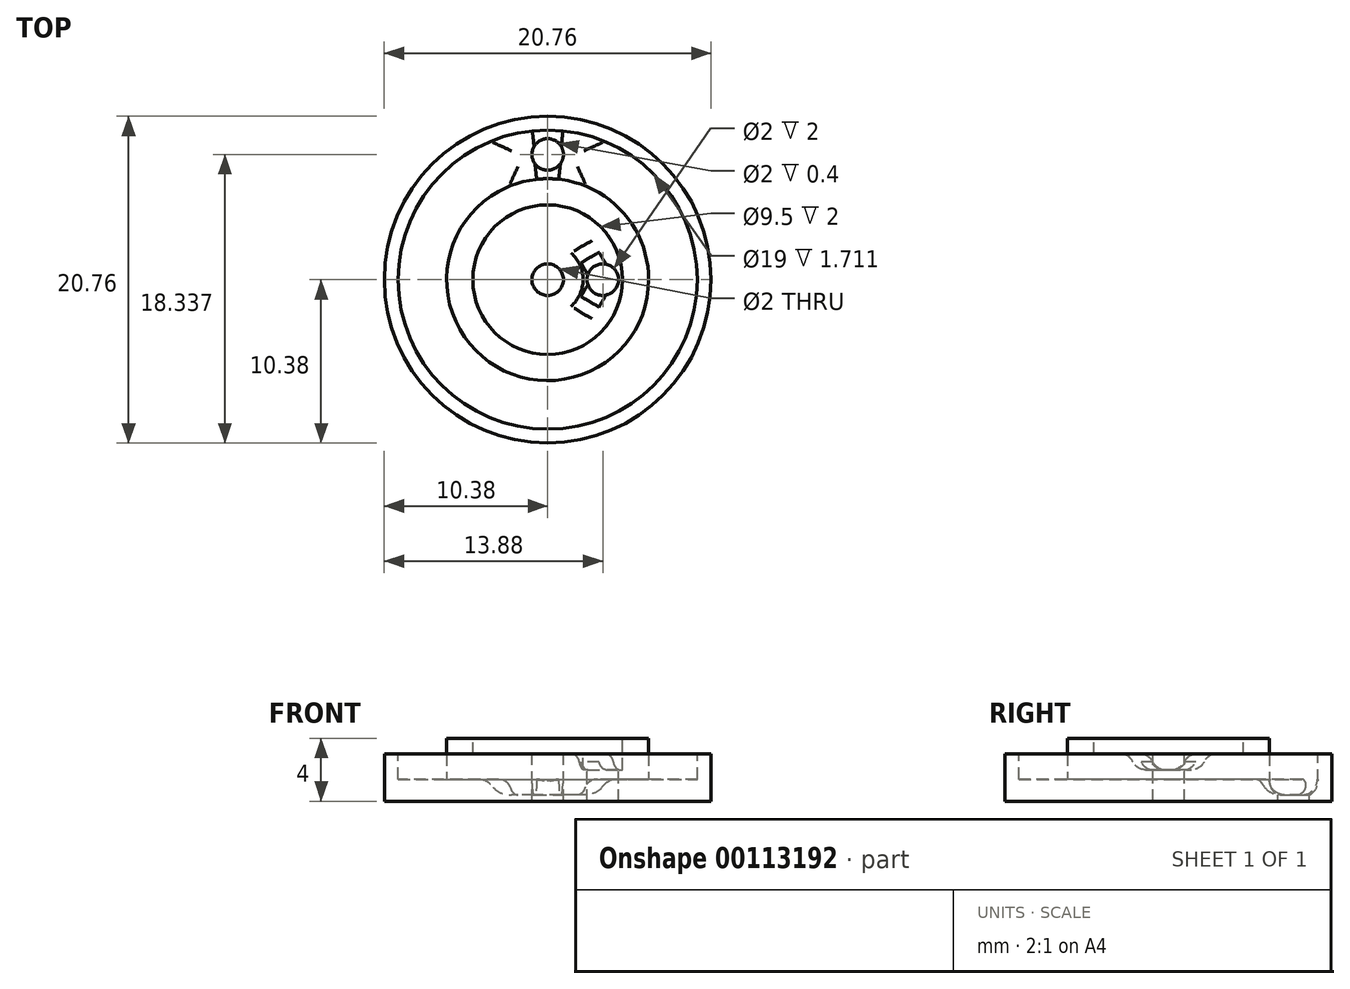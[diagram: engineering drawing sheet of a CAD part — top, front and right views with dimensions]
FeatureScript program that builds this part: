
annotation { "Feature Type Name" : "Feature", "Feature Type Description" : "" }
export const myFeature = defineFeature(function(context is Context, id is Id, definition is map)
    precondition{}
    {
        {
            var Q0;
            Q0=qCreatedBy(makeId("Top.planeOp"),FACE);
            var sketch = newSketch(context, id + "F0", { "sketchPlane" : qUnion([Q0])});
            skCircle(sketch, "E0", {"center": v(0, 0) * mm, "radius": 10.38 * mm});
            skSolve(sketch);
        }
        {
            var Q0;
            Q0=makeQuery(id+"F0.imprint","IMPRINT",FACE,{"disambiguationData":[TD([[makeQuery(id+"F0.imprint","IMPRINT",EDGE,{"derivedFrom":sQuery(id+"F0.wireOp",EDGE,"E0")}),1.0]])]});
            extrude(context, id + "F1", {"entities" : qUnion([Q0]), "depth" : 3 * mm});
        }
        {
            var Q0;
            Q0=makeQuery(id+"F1.opExtrude","CAP_FACE",FACE,{"disambiguationData":[OSD([sQuery(id+"F0.wireOp",EDGE,"E0")])],"isStart":false});
            var sketch = newSketch(context, id + "F2", { "sketchPlane" : qUnion([Q0])});
            skCircle(sketch, "E1", {"center": v(0, 0) * mm, "radius": 9.5 * mm});
            skCircle(sketch, "E2", {"center": v(0, 0) * mm, "radius": 6.41 * mm});
            skCircle(sketch, "E3", {"center": v(0, 0) * mm, "radius": 4.75 * mm});
            skSolve(sketch);
        }
        {
            var Q0;
            Q0=makeQuery(id+"F2.imprint","IMPRINT",FACE,{"disambiguationData":[TD([[makeQuery(id+"F2.imprint","IMPRINT",EDGE,{"derivedFrom":sQuery(id+"F2.wireOp",EDGE,"E2")}),1.0]])]});
            var Q1;
            Q1=makeQuery(id+"F2.imprint","IMPRINT",FACE,{"disambiguationData":[TD([[makeQuery(id+"F2.imprint","IMPRINT",EDGE,{"derivedFrom":sQuery(id+"F2.wireOp",EDGE,"E3")}),1.0]])]});
            extrude(context, id + "F3", {"entities" : qUnion([Q0, Q1]), "operationType" : NewBodyOperationType.ADD, "depth" : 1 * mm});
        }
        {
            var Q0;
            Q0=makeQuery(id+"F3.opExtrude","CAP_FACE",FACE,{"disambiguationData":[OSD([sQuery(id+"F2.wireOp",EDGE,"E2")])],"isStart":false});
            var sketch = newSketch(context, id + "F4", { "sketchPlane" : qUnion([Q0])});
            skCircle(sketch, "E4.0", {"center": v(0, 0) * mm, "radius": 4.75 * mm});
            skSolve(sketch);
        }
        {
            var Q0;
            Q0=makeQuery(id+"F4.imprint","IMPRINT",FACE,{"disambiguationData":[TD([[makeQuery(id+"F4.imprint","IMPRINT",EDGE,{"derivedFrom":sQuery(id+"F4.wireOp",EDGE,"E4.0")}),1.0]])]});
            extrude(context, id + "F5", {"entities" : qUnion([Q0]), "operationType" : NewBodyOperationType.REMOVE, "oppositeDirection" : true, "depth" : 1 * mm});
        }
        {
            var Q0;
            Q0 = qSketchRegion(id + "F2", true);
            extrude(context, id + "F6", {"entities" : qUnion([Q0]), "operationType" : NewBodyOperationType.REMOVE, "oppositeDirection" : true, "depth" : 1.6 * mm});
        }
        {
            var Q0;
            Q0=makeQuery(id+"F5.boolean.opBoolean","COPY",FACE,{"derivedFrom":makeQuery(id+"F5.opExtrude","CAP_FACE",FACE,{"disambiguationData":[OSD([sQuery(id+"F4.wireOp",EDGE,"E4.0")])],"isStart":false})});
            var sketch = newSketch(context, id + "F7", { "sketchPlane" : qUnion([Q0])});
            skCircle(sketch, "E5", {"center": v(0, 0) * mm, "radius": 1 * mm});
            skSolve(sketch);
        }
        {
            var Q0;
            Q0 = qSketchRegion(id + "F7", true);
            extrude(context, id + "F8", {"entities" : qUnion([Q0]), "operationType" : NewBodyOperationType.REMOVE, "endBound" : BoundingType.THROUGH_ALL, "oppositeDirection" : true, "depth" : 25 * mm});
        }
        {
            var Q0;
            Q0=makeQuery(id+"F6.boolean.opBoolean","COPY",FACE,{"derivedFrom":makeQuery(id+"F6.opExtrude","CAP_FACE",FACE,{"disambiguationData":[OSD([sQuery(id+"F2.wireOp",EDGE,"E1"),sQuery(id+"F2.wireOp",EDGE,"E2")])],"isStart":false})});
            var sketch = newSketch(context, id + "F9", { "sketchPlane" : qUnion([Q0])});
            skLineSegment(sketch, "E6", {"start": v(0, 9.5) * mm, "end": v(0, 6.41) * mm, "construction": true});
            skCircle(sketch, "E7", {"center": v(0, 7.96) * mm, "radius": 1 * mm});
            skSolve(sketch);
        }
        {
            var Q0;
            Q0 = qSketchRegion(id + "F9", true);
            extrude(context, id + "F10", {"entities" : qUnion([Q0]), "operationType" : NewBodyOperationType.REMOVE, "endBound" : BoundingType.THROUGH_ALL, "oppositeDirection" : true, "depth" : 25 * mm});
        }
        {
            var Q0;
            Q0=makeQuery(id+"F5.boolean.opBoolean","COPY",FACE,{"derivedFrom":makeQuery(id+"F5.opExtrude","CAP_FACE",FACE,{"disambiguationData":[OSD([sQuery(id+"F4.wireOp",EDGE,"E4.0")])],"isStart":false})});
            var sketch = newSketch(context, id + "F11", { "sketchPlane" : qUnion([Q0])});
            skLineSegment(sketch, "E8", {"start": v(2.25, 0) * mm, "end": v(4.75, 0) * mm, "construction": true});
            skCircle(sketch, "E9", {"center": v(3.5, 0) * mm, "radius": 1 * mm});
            skSolve(sketch);
        }
        {
            var Q0;
            Q0 = qSketchRegion(id + "F11", true);
            extrude(context, id + "F12", {"entities" : qUnion([Q0]), "operationType" : NewBodyOperationType.REMOVE, "endBound" : BoundingType.THROUGH_ALL, "oppositeDirection" : true, "depth" : 25 * mm});
        }
        {
            var Q0;
            Q0=makeQuery(id+"F6.boolean.opBoolean","COPY",FACE,{"derivedFrom":makeQuery(id+"F6.opExtrude","CAP_FACE",FACE,{"disambiguationData":[OSD([sQuery(id+"F2.wireOp",EDGE,"E1"),sQuery(id+"F2.wireOp",EDGE,"E2")])],"isStart":false})});
            var sketch = newSketch(context, id + "F13", { "sketchPlane" : qUnion([Q0])});
            skLineSegment(sketch, "E10", {"start": v(3.64, 8.78) * mm, "end": v(2.45, 5.93) * mm});
            skLineSegment(sketch, "E11", {"start": v(0, 0) * mm, "end": v(-2.45, 5.93) * mm, "construction": true});
            skLineSegment(sketch, "E12", {"start": v(0, 0) * mm, "end": v(0, 8.78) * mm, "construction": true});
            skLineSegment(sketch, "E13", {"start": v(3.64, 8.78) * mm, "end": v(-3.64, 8.78) * mm, "construction": true});
            skLineSegment(sketch, "E14", {"start": v(2.45, 5.93) * mm, "end": v(0, 0) * mm, "construction": true});
            skLineSegment(sketch, "E15", {"start": v(-2.45, 5.93) * mm, "end": v(-3.64, 8.78) * mm});
            skArc(sketch, "E16", {"start": v(3.64, 8.78) * mm, "mid": v(0, 9.5) * mm, "end": v(-3.64, 8.78) * mm});
            skArc(sketch, "E17", {"start": v(-3.64, 8.78) * mm, "mid": v(0, -9.5) * mm, "end": v(3.64, 8.78) * mm, "construction": true});
            skArc(sketch, "E18", {"start": v(-2.45, 5.93) * mm, "mid": v(0, -6.41) * mm, "end": v(2.45, 5.93) * mm, "construction": true});
            skArc(sketch, "E19", {"start": v(2.45, 5.93) * mm, "mid": v(0, 6.41) * mm, "end": v(-2.45, 5.93) * mm});
            skSolve(sketch);
        }
        {
            var Q0;
            Q0=makeQuery(id+"F13.imprint","IMPRINT",FACE,{"disambiguationData":[TD([[makeQuery(id+"F13.imprint","IMPRINT",EDGE,{"derivedFrom":sQuery(id+"F13.wireOp",EDGE,"E10")}),-1.0]])]});
            extrude(context, id + "F14", {"entities" : qUnion([Q0]), "operationType" : NewBodyOperationType.REMOVE, "oppositeDirection" : true, "depth" : 1 * mm});
        }
        {
            var Q0;
            Q0=makeQuery(id+"F5.boolean.opBoolean","COPY",FACE,{"derivedFrom":makeQuery(id+"F5.opExtrude","CAP_FACE",FACE,{"disambiguationData":[OSD([sQuery(id+"F4.wireOp",EDGE,"E4.0")])],"isStart":false})});
            var sketch = newSketch(context, id + "F15", { "sketchPlane" : qUnion([Q0])});
            skCircle(sketch, "E20.0", {"center": v(0, 0) * mm, "radius": 9.5 * mm});
            skCircle(sketch, "E20.1", {"center": v(0, 0) * mm, "radius": 6.41 * mm});
            skLineSegment(sketch, "E21", {"start": v(4.75, 0) * mm, "end": v(2.25, 0) * mm, "construction": true});
            skPoint(sketch, "E22", {"position": v(3.5, 0) * mm});
            skLineSegment(sketch, "E23", {"start": v(4.11, 2.38) * mm, "end": v(1.95, 1.12) * mm});
            skLineSegment(sketch, "E24", {"start": v(0, 0) * mm, "end": v(1.95, -1.12) * mm, "construction": true});
            skLineSegment(sketch, "E25", {"start": v(4.11, -2.37) * mm, "end": v(4.11, 2.37) * mm, "construction": true});
            skLineSegment(sketch, "E26", {"start": v(4.11, 0) * mm, "end": v(0, 0) * mm, "construction": true});
            skArc(sketch, "E27", {"start": v(4.11, 2.37) * mm, "mid": v(-4.75, 0) * mm, "end": v(4.11, -2.38) * mm, "construction": true});
            skArc(sketch, "E28", {"start": v(4.11, -2.37) * mm, "mid": v(4.75, 0) * mm, "end": v(4.11, 2.37) * mm});
            skArc(sketch, "E29", {"start": v(1.95, -1.12) * mm, "mid": v(2.25, 0) * mm, "end": v(1.95, 1.12) * mm});
            skArc(sketch, "E30", {"start": v(1.95, 1.12) * mm, "mid": v(-2.25, 0) * mm, "end": v(1.95, -1.12) * mm, "construction": true});
            skLineSegment(sketch, "E31", {"start": v(1.95, 1.12) * mm, "end": v(0, 0) * mm, "construction": true});
            skLineSegment(sketch, "E32", {"start": v(1.95, -1.12) * mm, "end": v(4.11, -2.37) * mm});
            skSolve(sketch);
        }
        {
            var Q0;
            Q0=makeQuery(id+"F15.imprint","IMPRINT",FACE,{"disambiguationData":[TD([[makeQuery(id+"F15.imprint","IMPRINT",EDGE,{"derivedFrom":sQuery(id+"F15.wireOp",EDGE,"E23")}),1.0]])]});
            extrude(context, id + "F16", {"entities" : qUnion([Q0]), "operationType" : NewBodyOperationType.REMOVE, "oppositeDirection" : true, "depth" : 1 * mm});
        }
        {
            var Q0;
            Q0=makeQuery(id+"F14.boolean.opBoolean","COPY",EDGE,{"derivedFrom":makeQuery(id+"F14.opExtrude","CAP_EDGE",EDGE,{"disambiguationData":[OSD([sQuery(id+"F13.wireOp",EDGE,"E10")])],"isStart":false})});
            var Q1;
            Q1=makeQuery(id+"F14.boolean.opBoolean","COPY",EDGE,{"derivedFrom":makeQuery(id+"F14.opExtrude","CAP_EDGE",EDGE,{"disambiguationData":[OSD([sQuery(id+"F13.wireOp",EDGE,"E16")])],"isStart":false})});
            var Q2;
            Q2=makeQuery(id+"F14.boolean.opBoolean","COPY",EDGE,{"derivedFrom":makeQuery(id+"F14.opExtrude","CAP_EDGE",EDGE,{"disambiguationData":[OSD([sQuery(id+"F13.wireOp",EDGE,"E19")])],"isStart":false})});
            var Q3;
            Q3=makeQuery(id+"F14.boolean.opBoolean","COPY",EDGE,{"derivedFrom":makeQuery(id+"F14.opExtrude","CAP_EDGE",EDGE,{"disambiguationData":[OSD([sQuery(id+"F13.wireOp",EDGE,"E15")])],"isStart":false})});
            var Q4;
            Q4=makeQuery(id+"F16.boolean.opBoolean","COPY",EDGE,{"derivedFrom":makeQuery(id+"F16.opExtrude","CAP_EDGE",EDGE,{"disambiguationData":[OSD([sQuery(id+"F15.wireOp",EDGE,"E32")])],"isStart":false})});
            var Q5;
            Q5=makeQuery(id+"F16.boolean.opBoolean","COPY",EDGE,{"derivedFrom":makeQuery(id+"F16.opExtrude","CAP_EDGE",EDGE,{"disambiguationData":[OSD([sQuery(id+"F15.wireOp",EDGE,"E23")])],"isStart":false})});
            fillet(context, id + "F17", {"entities" : qUnion([Q0, Q1, Q2, Q3, Q4, Q5]), "radius" : 1 * mm, "tangentPropagation" : true, "allowEdgeOverflow" : false});
        }
        {
            var Q0;
            Q0=makeQuery(id+"F17.opFillet","BLEND_EDGE",EDGE,{"blendedFrom":[makeQuery(id+"F14.boolean.opBoolean","COPY",EDGE,{"derivedFrom":makeQuery(id+"F14.opExtrude","CAP_EDGE",EDGE,{"disambiguationData":[OSD([sQuery(id+"F13.wireOp",EDGE,"E10")])],"isStart":false})}),makeQuery(id+"F6.boolean.opBoolean","COPY",FACE,{"derivedFrom":makeQuery(id+"F6.opExtrude","CAP_FACE",FACE,{"disambiguationData":[OSD([sQuery(id+"F2.wireOp",EDGE,"E1"),sQuery(id+"F2.wireOp",EDGE,"E2")])],"isStart":false})})],"blendedInto":[makeQuery(id+"F6.boolean.opBoolean","COPY",FACE,{"derivedFrom":makeQuery(id+"F6.opExtrude","CAP_FACE",FACE,{"disambiguationData":[OSD([sQuery(id+"F2.wireOp",EDGE,"E1"),sQuery(id+"F2.wireOp",EDGE,"E2")])],"isStart":false})})]});
            var Q1;
            Q1=makeQuery(id+"F17.opFillet","BLEND_EDGE",EDGE,{"blendedFrom":[makeQuery(id+"F14.boolean.opBoolean","COPY",EDGE,{"derivedFrom":makeQuery(id+"F14.opExtrude","CAP_EDGE",EDGE,{"disambiguationData":[OSD([sQuery(id+"F13.wireOp",EDGE,"E15")])],"isStart":false})}),makeQuery(id+"F6.boolean.opBoolean","COPY",FACE,{"derivedFrom":makeQuery(id+"F6.opExtrude","CAP_FACE",FACE,{"disambiguationData":[OSD([sQuery(id+"F2.wireOp",EDGE,"E1"),sQuery(id+"F2.wireOp",EDGE,"E2")])],"isStart":false})})],"blendedInto":[makeQuery(id+"F6.boolean.opBoolean","COPY",FACE,{"derivedFrom":makeQuery(id+"F6.opExtrude","CAP_FACE",FACE,{"disambiguationData":[OSD([sQuery(id+"F2.wireOp",EDGE,"E1"),sQuery(id+"F2.wireOp",EDGE,"E2")])],"isStart":false})})]});
            var Q2;
            Q2=makeQuery(id+"F17.opFillet","BLEND_EDGE",EDGE,{"blendedFrom":[makeQuery(id+"F16.boolean.opBoolean","COPY",EDGE,{"derivedFrom":makeQuery(id+"F16.opExtrude","CAP_EDGE",EDGE,{"disambiguationData":[OSD([sQuery(id+"F15.wireOp",EDGE,"E23")])],"isStart":false})}),makeQuery(id+"F5.boolean.opBoolean","COPY",FACE,{"derivedFrom":makeQuery(id+"F5.opExtrude","CAP_FACE",FACE,{"disambiguationData":[OSD([sQuery(id+"F4.wireOp",EDGE,"E4.0")])],"isStart":false})})],"blendedInto":[makeQuery(id+"F5.boolean.opBoolean","COPY",FACE,{"derivedFrom":makeQuery(id+"F5.opExtrude","CAP_FACE",FACE,{"disambiguationData":[OSD([sQuery(id+"F4.wireOp",EDGE,"E4.0")])],"isStart":false})})]});
            var Q3;
            Q3=makeQuery(id+"F17.opFillet","BLEND_EDGE",EDGE,{"blendedFrom":[makeQuery(id+"F16.boolean.opBoolean","COPY",EDGE,{"derivedFrom":makeQuery(id+"F16.opExtrude","CAP_EDGE",EDGE,{"disambiguationData":[OSD([sQuery(id+"F15.wireOp",EDGE,"E32")])],"isStart":false})}),makeQuery(id+"F5.boolean.opBoolean","COPY",FACE,{"derivedFrom":makeQuery(id+"F5.opExtrude","CAP_FACE",FACE,{"disambiguationData":[OSD([sQuery(id+"F4.wireOp",EDGE,"E4.0")])],"isStart":false})})],"blendedInto":[makeQuery(id+"F5.boolean.opBoolean","COPY",FACE,{"derivedFrom":makeQuery(id+"F5.opExtrude","CAP_FACE",FACE,{"disambiguationData":[OSD([sQuery(id+"F4.wireOp",EDGE,"E4.0")])],"isStart":false})})]});
            fillet(context, id + "F18", {"entities" : qUnion([Q0, Q1, Q2, Q3]), "radius" : 1 * mm, "tangentPropagation" : true, "allowEdgeOverflow" : false});
        }
    });
